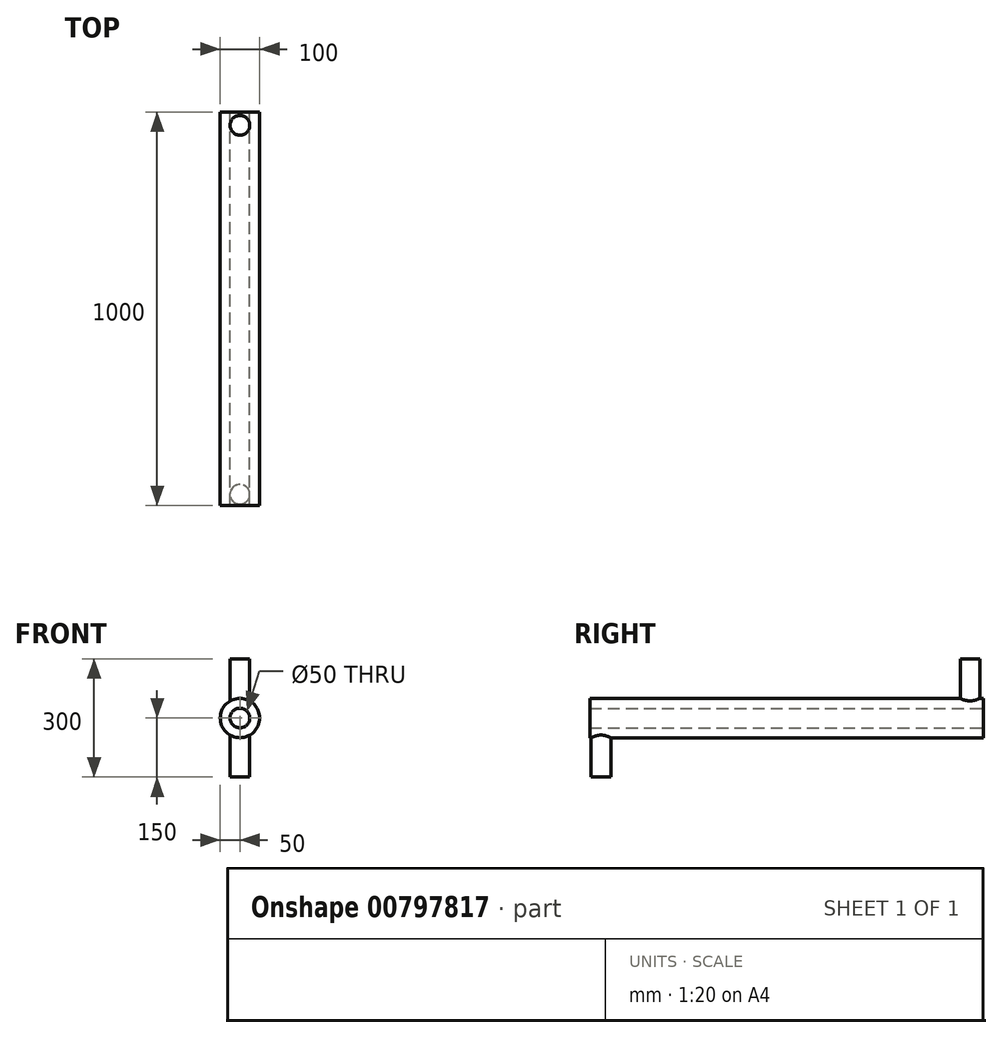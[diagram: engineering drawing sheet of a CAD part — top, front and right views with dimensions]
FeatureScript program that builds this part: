
annotation { "Feature Type Name" : "Feature", "Feature Type Description" : "" }
export const myFeature = defineFeature(function(context is Context, id is Id, definition is map)
    precondition{}
    {
        {
            var Q0;
            Q0=qCreatedBy(makeId("Front.planeOp"),FACE);
            var sketch = newSketch(context, id + "F0", { "sketchPlane" : qUnion([Q0])});
            skCircle(sketch, "E0", {"center": v(0, 0) * mm, "radius": 50 * mm});
            skCircle(sketch, "E1", {"center": v(0, 0) * mm, "radius": 25 * mm});
            skSolve(sketch);
        }
        {
            var Q0;
            Q0=qCreatedBy(makeId("Top.planeOp"),FACE);
            cPlane(context, id + "F1", {"entities" : qUnion([Q0]), "cplaneType" : CPlaneType.OFFSET, "offset" : 25 * mm, "width" : 150 * mm, "height" : 150 * mm});
        }
        {
            var Q0;
            Q0=qCreatedBy(makeId("Top.planeOp"),FACE);
            cPlane(context, id + "F2", {"entities" : qUnion([Q0]), "cplaneType" : CPlaneType.OFFSET, "offset" : 25 * mm, "oppositeDirection" : true, "width" : 150 * mm, "height" : 150 * mm});
        }
        {
            var Q0;
            Q0=makeQuery(id+"F0.imprint","IMPRINT",FACE,{"disambiguationData":[TD([[makeQuery(id+"F0.imprint","IMPRINT",EDGE,{"derivedFrom":sQuery(id+"F0.wireOp",EDGE,"E0")}),1.0]])]});
            extrude(context, id + "F3", {"entities" : qUnion([Q0]), "depth" : 1000 * mm, "offsetDistance" : 25 * mm});
        }
        {
            var Q0;
            Q0=qCreatedBy(id+"F2.planeOp",FACE);
            var sketch = newSketch(context, id + "F4", { "sketchPlane" : qUnion([Q0])});
            skCircle(sketch, "E2", {"center": v(0, -971.54) * mm, "radius": 25 * mm});
            skSolve(sketch);
        }
        {
            var Q0;
            Q0 = qSketchRegion(id + "F4", true);
            extrude(context, id + "F5", {"entities" : qUnion([Q0]), "operationType" : NewBodyOperationType.ADD, "oppositeDirection" : true, "depth" : 125 * mm, "offsetDistance" : 25 * mm});
        }
        {
            var Q0;
            Q0=qCreatedBy(id+"F1.planeOp",FACE);
            var sketch = newSketch(context, id + "F6", { "sketchPlane" : qUnion([Q0])});
            skCircle(sketch, "E3", {"center": v(0, -34.05) * mm, "radius": 25 * mm});
            skSolve(sketch);
        }
        {
            var Q0;
            Q0 = qSketchRegion(id + "F6", true);
            extrude(context, id + "F7", {"entities" : qUnion([Q0]), "operationType" : NewBodyOperationType.ADD, "depth" : 125 * mm, "offsetDistance" : 25 * mm});
        }
    });
